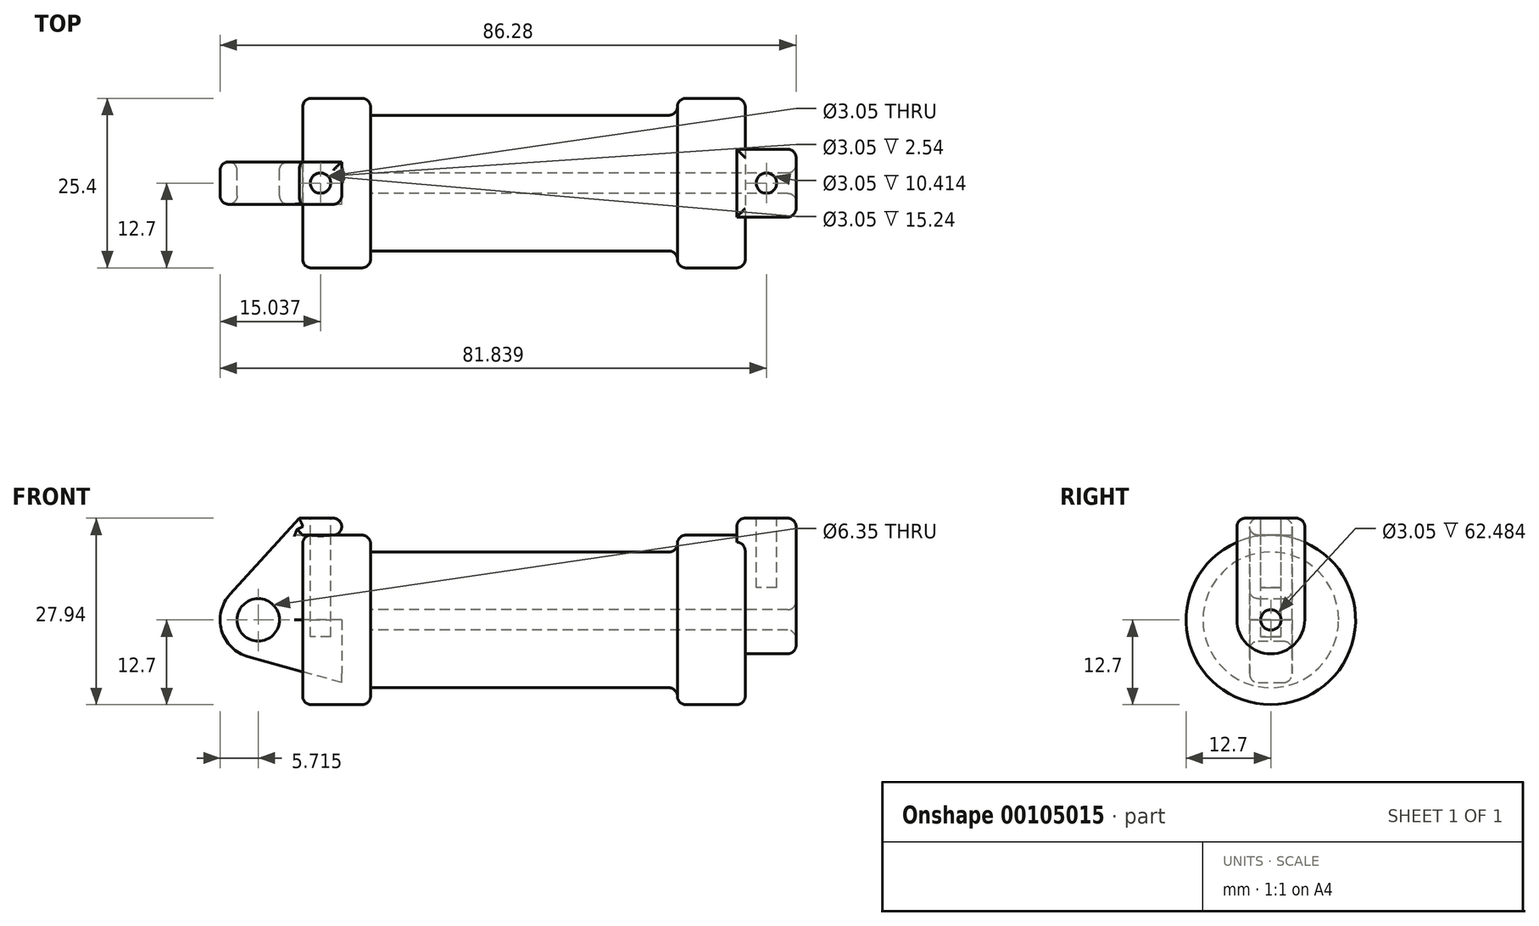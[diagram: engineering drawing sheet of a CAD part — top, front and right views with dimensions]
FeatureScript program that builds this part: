
annotation { "Feature Type Name" : "Feature", "Feature Type Description" : "" }
export const myFeature = defineFeature(function(context is Context, id is Id, definition is map)
    precondition{}
    {
        {
            var Q0;
            Q0=qCreatedBy(makeId("Front.planeOp"),FACE);
            var sketch = newSketch(context, id + "F0", { "sketchPlane" : qUnion([Q0])});
            skLineSegment(sketch, "E0", {"start": v(0, 0) * mm, "end": v(0, 12.7) * mm});
            skLineSegment(sketch, "E1", {"start": v(0, 12.7) * mm, "end": v(10.16, 12.7) * mm});
            skLineSegment(sketch, "E2", {"start": v(10.16, 12.7) * mm, "end": v(10.16, 10.16) * mm});
            skLineSegment(sketch, "E3", {"start": v(10.16, 10.16) * mm, "end": v(56.13, 10.16) * mm});
            skLineSegment(sketch, "E4", {"start": v(56.13, 10.16) * mm, "end": v(56.13, 12.7) * mm});
            skLineSegment(sketch, "E5", {"start": v(56.13, 12.7) * mm, "end": v(66.3, 12.7) * mm});
            skLineSegment(sketch, "E6", {"start": v(66.3, 12.7) * mm, "end": v(66.3, 0) * mm});
            skLineSegment(sketch, "E7", {"start": v(66.3, 0) * mm, "end": v(0, 0) * mm});
            skLineSegment(sketch, "E8", {"start": v(5.84, 15.24) * mm, "end": v(-0.5, 15.24) * mm});
            skLineSegment(sketch, "E9", {"start": v(-0.5, 15.24) * mm, "end": v(-10.88, 3.85) * mm});
            skLineSegment(sketch, "E10", {"start": v(0, 0) * mm, "end": v(-6.65, 0) * mm});
            skCircle(sketch, "E11", {"center": v(-6.65, 0) * mm, "radius": 5.72 * mm});
            skCircle(sketch, "E12", {"center": v(-6.65, 0) * mm, "radius": 3.18 * mm});
            skLineSegment(sketch, "E13", {"start": v(5.84, 15.24) * mm, "end": v(5.84, -9.4) * mm});
            skLineSegment(sketch, "E14", {"start": v(5.84, -9.4) * mm, "end": v(-8.18, -5.5) * mm});
            skSolve(sketch);
        }
        {
            var Q0;
            {var subQ0=sQuery(id+"F0.wireOp",EDGE,"E2");Q0=makeQuery(id+"F0.imprint","IMPRINT",FACE,{"disambiguationData":[TD([[makeQuery(id+"F0.imprint","IMPRINT",EDGE,{"derivedFrom":subQ0}),-1.0]])]});}
            var Q1;
            {var subQ0=sQuery(id+"F0.wireOp",EDGE,"E0");Q1=makeQuery(id+"F0.imprint","IMPRINT",FACE,{"disambiguationData":[TD([[makeQuery(id+"F0.imprint","IMPRINT",EDGE,{"derivedFrom":subQ0}),-1.0]])]});}
            var Q2;
            Q2=sQuery(id+"F0.wireOp",EDGE,"E7");
            revolve(context, id + "F1", {"entities" : qUnion([Q0, Q1]), "axis" : qUnion([Q2]), "revolveType" : RevolveType.FULL});
        }
        {
            var Q0;
            {var subQ3=sQuery(id+"F0.wireOp",EDGE,"E0");Q0=makeQuery(id+"F0.imprint","IMPRINT",FACE,{"disambiguationData":[TD([[makeQuery(id+"F0.imprint","IMPRINT",EDGE,{"derivedFrom":subQ3}),1.0]])]});}
            var Q1;
            {var subQ4=sQuery(id+"F0.wireOp",EDGE,"E12");Q1=makeQuery(id+"F0.imprint","IMPRINT",FACE,{"disambiguationData":[TD([[makeQuery(id+"F0.imprint","IMPRINT",EDGE,{"derivedFrom":subQ4}),-1.0]])]});}
            var Q2;
            {var subQ0=sQuery(id+"F0.wireOp",EDGE,"E14");Q2=makeQuery(id+"F0.imprint","IMPRINT",FACE,{"disambiguationData":[TD([[makeQuery(id+"F0.imprint","IMPRINT",EDGE,{"derivedFrom":subQ0}),-1.0]])]});}
            extrude(context, id + "F2", {"entities" : qUnion([Q0, Q1, Q2]), "endBound" : BoundingType.SYMMETRIC, "depth" : 6.35 * mm});
        }
        {
            var Q0;
            Q0=makeQuery(id+"F1.opRevolve","SWEPT_FACE",FACE,{"disambiguationData":[OSD([sQuery(id+"F0.wireOp",EDGE,"E6")])]});
            var sketch = newSketch(context, id + "F3", { "sketchPlane" : qUnion([Q0])});
            skCircle(sketch, "E15", {"center": v(0, 0) * mm, "radius": 1.52 * mm});
            skCircle(sketch, "E16", {"center": v(0, 0) * mm, "radius": 5.08 * mm});
            skLineSegment(sketch, "E17", {"start": v(5.08, 0) * mm, "end": v(5.08, 15.24) * mm});
            skLineSegment(sketch, "E18", {"start": v(-5.08, 0) * mm, "end": v(-5.08, 15.24) * mm});
            skLineSegment(sketch, "E19", {"start": v(-5.08, 15.24) * mm, "end": v(5.08, 15.24) * mm});
            skSolve(sketch);
        }
        {
            var Q0;
            {var subQ0=sQuery(id+"F3.wireOp",EDGE,"E19");Q0=makeQuery(id+"F3.imprint","IMPRINT",FACE,{"disambiguationData":[TD([[makeQuery(id+"F3.imprint","IMPRINT",EDGE,{"derivedFrom":subQ0}),-1.0]])]});}
            extrude(context, id + "F4", {"entities" : qUnion([Q0]), "operationType" : NewBodyOperationType.ADD, "depth" : 7.62 * mm, "hasSecondDirection" : true, "secondDirectionOppositeDirection" : true, "secondDirectionDepth" : 1.27 * mm});
        }
        {
            var Q0;
            Q0=makeQuery(id+"F3.imprint","IMPRINT",FACE,{"disambiguationData":[TD([[makeQuery(id+"F3.imprint","IMPRINT",EDGE,{"derivedFrom":sQuery(id+"F3.wireOp",EDGE,"E15")}),-1.0]])]});
            var Q1;
            {var subQ0=sQuery(id+"F3.wireOp",EDGE,"E19");Q1=makeQuery(id+"F3.imprint","IMPRINT",FACE,{"disambiguationData":[TD([[makeQuery(id+"F3.imprint","IMPRINT",EDGE,{"derivedFrom":subQ0}),-1.0]])]});}
            var Q2;
            {var subQ0=sQuery(id+"F3.wireOp",EDGE,"E17");var subQ1=sQuery(id+"F3.wireOp",EDGE,"E16");var subQ2=makeQuery(id+"F3.imprint","INTERSECT",VERTEX,{"derivedFrom":[subQ1,subQ0]});Q2=makeQuery(id+"F3.imprint","IMPRINT",FACE,{"disambiguationData":[TD([[makeQuery(id+"F3.imprint","IMPRINT",EDGE,{"disambiguationData":[TD([[subQ2,-1.0]])],"derivedFrom":subQ1}),-1.0]])]});}
            extrude(context, id + "F5", {"entities" : qUnion([Q0, Q1, Q2]), "operationType" : NewBodyOperationType.ADD, "depth" : 7.62 * mm});
        }
        {
            var Q0;
            Q0=makeQuery(id+"F4.opExtrude","SWEPT_FACE",FACE,{"disambiguationData":[OSD([sQuery(id+"F3.wireOp",EDGE,"E19")])]});
            var sketch = newSketch(context, id + "F6", { "sketchPlane" : qUnion([Q0])});
            skLineSegment(sketch, "E20", {"start": v(69.47, -5.08) * mm, "end": v(69.47, 5.08) * mm, "construction": true});
            skLineSegment(sketch, "E21", {"start": v(73.91, 0) * mm, "end": v(65.02, 0) * mm, "construction": true});
            skCircle(sketch, "E22", {"center": v(69.47, 0) * mm, "radius": 1.52 * mm});
            skSolve(sketch);
        }
        {
            var Q0;
            Q0 = qSketchRegion(id + "F6", true);
            extrude(context, id + "F7", {"entities" : qUnion([Q0]), "operationType" : NewBodyOperationType.REMOVE, "oppositeDirection" : true, "depth" : 10.4 * mm});
        }
        {
            var Q0;
            Q0=makeQuery(id+"F2.opExtrude","SWEPT_FACE",FACE,{"disambiguationData":[OSD([sQuery(id+"F0.wireOp",EDGE,"E8")])]});
            var sketch = newSketch(context, id + "F8", { "sketchPlane" : qUnion([Q0])});
            skLineSegment(sketch, "E23", {"start": v(2.67, 3.18) * mm, "end": v(2.67, -3.18) * mm, "construction": true});
            skLineSegment(sketch, "E24", {"start": v(5.84, 0) * mm, "end": v(-0.5, 0) * mm, "construction": true});
            skCircle(sketch, "E25", {"center": v(2.67, 0) * mm, "radius": 1.52 * mm});
            skSolve(sketch);
        }
        {
            var Q0;
            Q0=makeQuery(id+"F8.imprint","IMPRINT",FACE,{"disambiguationData":[TD([[makeQuery(id+"F8.imprint","IMPRINT",EDGE,{"derivedFrom":sQuery(id+"F8.wireOp",EDGE,"E25")}),1.0]])]});
            var Q1;
            Q1=sQuery(id+"F8.wireOp",EDGE,"E25");
            extrude(context, id + "F9", {"entities" : qUnion([Q0]), "operationType" : NewBodyOperationType.REMOVE, "surfaceEntities" : qUnion([Q1]), "oppositeDirection" : true, "depth" : 17.78 * mm});
        }
        {
            var Q0;
            Q0=makeQuery(id+"F2.opExtrude","CAP_EDGE",EDGE,{"disambiguationData":[OSD([sQuery(id+"F0.wireOp",EDGE,"E9")])],"isStart":false});
            var Q1;
            Q1=makeQuery(id+"F2.opExtrude","CAP_EDGE",EDGE,{"disambiguationData":[OSD([sQuery(id+"F0.wireOp",EDGE,"E9")])],"isStart":true});
            var Q2;
            Q2=makeQuery(id+"F2.opExtrude","CAP_EDGE",EDGE,{"disambiguationData":[OSD([sQuery(id+"F0.wireOp",EDGE,"E8")])],"isStart":false});
            var Q3;
            Q3=makeQuery(id+"F2.opExtrude","CAP_EDGE",EDGE,{"disambiguationData":[OSD([sQuery(id+"F0.wireOp",EDGE,"E8")])],"isStart":true});
            var Q4;
            Q4=makeQuery(id+"F2.opExtrude","SWEPT_EDGE",EDGE,{"disambiguationData":[OSD([sQuery(id+"F0.wireOp",EDGE,"E8"),sQuery(id+"F0.wireOp",EDGE,"E13")])]});
            var Q5;
            Q5=makeQuery(id+"F2.opExtrude","SWEPT_EDGE",EDGE,{"disambiguationData":[OSD([sQuery(id+"F0.wireOp",EDGE,"E1"),sQuery(id+"F0.wireOp",EDGE,"E13")])]});
            var Q6;
            {var subQ0=sQuery(id+"F0.wireOp",EDGE,"E13");Q6=makeQuery(id+"F2.opExtrude","CAP_EDGE",EDGE,{"disambiguationData":[OSD([subQ0]),TDD([makeQuery(id+"F0.imprint","IMPRINT",EDGE,{"disambiguationData":[TD([[makeQuery(id+"F0.imprint","INTERSECT",VERTEX,{"derivedFrom":[sQuery(id+"F0.wireOp",EDGE,"E8"),subQ0]}),-1.0]])],"derivedFrom":subQ0})])],"isStart":false});}
            var Q7;
            Q7=makeQuery(id+"F2.opExtrude","CAP_EDGE",EDGE,{"disambiguationData":[OSD([sQuery(id+"F0.wireOp",EDGE,"E1")])],"isStart":false});
            var Q8;
            Q8=makeQuery(id+"F2.opExtrude","CAP_EDGE",EDGE,{"disambiguationData":[OSD([sQuery(id+"F0.wireOp",EDGE,"E0")])],"isStart":false});
            var Q9;
            Q9=makeQuery(id+"F1.opRevolve","SWEPT_EDGE",EDGE,{"disambiguationData":[OSD([sQuery(id+"F0.wireOp",EDGE,"E0"),sQuery(id+"F0.wireOp",EDGE,"E1")])]});
            var Q10;
            Q10=makeQuery(id+"F1.opRevolve","SWEPT_EDGE",EDGE,{"disambiguationData":[OSD([sQuery(id+"F0.wireOp",EDGE,"E1"),sQuery(id+"F0.wireOp",EDGE,"E2")])]});
            var Q11;
            Q11=makeQuery(id+"F2.opExtrude","CAP_EDGE",EDGE,{"disambiguationData":[OSD([sQuery(id+"F0.wireOp",EDGE,"E0")])],"isStart":true});
            var Q12;
            Q12=makeQuery(id+"F2.opExtrude","CAP_EDGE",EDGE,{"disambiguationData":[OSD([sQuery(id+"F0.wireOp",EDGE,"E12")])],"isStart":true});
            var Q13;
            Q13=makeQuery(id+"F2.opExtrude","CAP_EDGE",EDGE,{"disambiguationData":[OSD([sQuery(id+"F0.wireOp",EDGE,"E12")])],"isStart":false});
            var Q14;
            {var subQ0=sQuery(id+"F3.wireOp",EDGE,"E18");Q14=makeQuery(id+"F5.boolean.opBoolean","MERGE",EDGE,{"derivedFrom":[makeQuery(id+"F4.opExtrude","CAP_EDGE",EDGE,{"disambiguationData":[OSD([subQ0])],"isStart":false}),makeQuery(id+"F5.opExtrude","CAP_EDGE",EDGE,{"disambiguationData":[OSD([subQ0])],"isStart":false})]});}
            var Q15;
            {var subQ0=sQuery(id+"F3.wireOp",EDGE,"E17");Q15=makeQuery(id+"F5.boolean.opBoolean","MERGE",EDGE,{"derivedFrom":[makeQuery(id+"F4.opExtrude","CAP_EDGE",EDGE,{"disambiguationData":[OSD([subQ0])],"isStart":false}),makeQuery(id+"F5.opExtrude","CAP_EDGE",EDGE,{"disambiguationData":[OSD([subQ0])],"isStart":false})]});}
            var Q16;
            Q16=makeQuery(id+"F4.opExtrude","CAP_EDGE",EDGE,{"disambiguationData":[OSD([sQuery(id+"F3.wireOp",EDGE,"E19")])],"isStart":false});
            var Q17;
            Q17=makeQuery(id+"F4.opExtrude","SWEPT_EDGE",EDGE,{"disambiguationData":[OSD([sQuery(id+"F3.wireOp",EDGE,"E18"),sQuery(id+"F3.wireOp",EDGE,"E19")])]});
            var Q18;
            Q18=makeQuery(id+"F5.opExtrude","CAP_EDGE",EDGE,{"disambiguationData":[OSD([sQuery(id+"F3.wireOp",EDGE,"E16")])],"isStart":false});
            var Q19;
            Q19=makeQuery(id+"F4.opExtrude","SWEPT_EDGE",EDGE,{"disambiguationData":[OSD([sQuery(id+"F3.wireOp",EDGE,"E17"),sQuery(id+"F3.wireOp",EDGE,"E19")])]});
            var Q20;
            Q20=makeQuery(id+"F4.opExtrude","CAP_EDGE",EDGE,{"disambiguationData":[OSD([sQuery(id+"F3.wireOp",EDGE,"E19")])],"isStart":true});
            var Q21;
            Q21=makeQuery(id+"F4.boolean.opBoolean","SPLIT",EDGE,{"disambiguationData":[OD(0.0)],"derivedFrom":makeQuery(id+"F1.opRevolve","SWEPT_EDGE",EDGE,{"disambiguationData":[OSD([sQuery(id+"F0.wireOp",EDGE,"E5"),sQuery(id+"F0.wireOp",EDGE,"E6")])]})});
            var Q22;
            Q22=makeQuery(id+"F1.opRevolve","SWEPT_EDGE",EDGE,{"disambiguationData":[OSD([sQuery(id+"F0.wireOp",EDGE,"E4"),sQuery(id+"F0.wireOp",EDGE,"E5")])]});
            var Q23;
            Q23=makeQuery(id+"F5.opExtrude","CAP_EDGE",EDGE,{"disambiguationData":[OSD([sQuery(id+"F3.wireOp",EDGE,"E15")])],"isStart":false});
            var Q24;
            Q24=makeQuery(id+"F7.boolean.opBoolean","COPY",EDGE,{"derivedFrom":makeQuery(id+"F7.opExtrude","CAP_EDGE",EDGE,{"disambiguationData":[OSD([sQuery(id+"F6.wireOp",EDGE,"E22")])],"isStart":true})});
            var Q25;
            Q25=makeQuery(id+"F1.opRevolve","SWEPT_EDGE",EDGE,{"disambiguationData":[OSD([sQuery(id+"F0.wireOp",EDGE,"E3"),sQuery(id+"F0.wireOp",EDGE,"E4")])]});
            fillet(context, id + "F10", {"entities" : qUnion([Q0, Q1, Q2, Q3, Q4, Q5, Q6, Q7, Q8, Q9, Q10, Q11, Q12, Q13, Q14, Q15, Q16, Q17, Q18, Q19, Q20, Q21, Q22, Q23, Q24, Q25]), "radius" : 1.27 * mm, "tangentPropagation" : true, "allowEdgeOverflow" : false});
        }
        {
            var Q0;
            Q0=makeQuery(id+"F5.boolean.opBoolean","SPLIT",FACE,{"disambiguationData":[TD([makeQuery(id+"F5.opExtrude","SWEPT_FACE",FACE,{"disambiguationData":[OSD([sQuery(id+"F3.wireOp",EDGE,"E15")])]})])],"derivedFrom":makeQuery(id+"F1.opRevolve","SWEPT_FACE",FACE,{"disambiguationData":[OSD([sQuery(id+"F0.wireOp",EDGE,"E6")])]})});
            var Q1;
            Q1=makeQuery(id+"F1.opRevolve","SWEPT_FACE",FACE,{"disambiguationData":[OSD([sQuery(id+"F0.wireOp",EDGE,"E2")])]});
            extrude(context, id + "F11", {"entities" : qUnion([Q0]), "operationType" : NewBodyOperationType.REMOVE, "endBound" : BoundingType.UP_TO_SURFACE, "oppositeDirection" : true, "endBoundEntityFace" : qUnion([Q1]), "depth" : 25.4 * mm});
        }
    });
